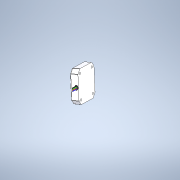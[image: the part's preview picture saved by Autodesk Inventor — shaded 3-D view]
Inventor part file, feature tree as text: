
AUTODESK INVENTOR PART (.ipt)
format: ipt  version: 2021 (Build 250183000, 183)  size: 951,296 bytes
history: native  units: mm
features: extrude x13, sketch x5, hole x4, fillet x4, plane x2, chamfer x2, pattern_linear x1, projected_geometry x1
ambient origin geometry x8: Origin, YZ Plane, XZ Plane, XY Plane, X Axis, Y Axis, Z Axis, Center Point
bodies: Solid1 (feature_tree)
feature tree (32):
  sketch  "Sketch1"  dims[d0=7.0mm d1=22.0mm]
  extrude  "Extrusion1"  Depth=22.0mm
  extrude  "Extrusion2"  Depth=31.0mm
  extrude  "Extrusion3"  Depth=3.0mm
  plane  "Work Plane2"
  extrude  "Extrusion7"  Depth=3.0mm
  extrude  "Extrusion8"  Depth=10.0mm
  chamfer  "Chamfer1"  Distance=42.0mm
  pattern_linear  "Rectangular Pattern2"  Spacing1=135.0deg  [1 undecoded]
  hole  "Hole1"  [1 undecoded]
  hole  "Hole2"  [1 undecoded]
  hole  "Hole3"  [1 undecoded]
  hole  "Hole4"  [1 undecoded]
  extrude  "Extrusion9"  Depth=10.0mm TaperAngle=0.0deg
  fillet  "Fillet1"  Radius=2.0mm
  fillet  "Fillet2"  Radius=48.0mm
  chamfer  "Chamfer2"  [1 undecoded]
  fillet  "Fillet3"  Radius=28.0mm
  sketch  "Sketch6"  dims[d10=3.0mm d11=3.0mm]
  extrude  "Extrusion10"  Depth=10.0mm
  fillet  "Fillet4"  Radius=1.0mm
  extrude  "Extrusion11"  Depth=10.0mm
  extrude  "Extrusion12"  Depth=10.0mm
  extrude  "Extrusion13"  Depth=10.0mm
  extrude  "Extrusion14"  Depth=10.0mm
  extrude  "Extrusion15"  Depth=10.0mm
  plane  "Work Plane3"
  extrude  "Extrusion16"  Depth=10.0mm
  sketch  "Sketch4"  dims[d4=5.0mm d5=31.0mm]
  projected_geometry  "Projected Loop2"
  sketch  "Sketch5"  dims[d6=31.0mm d9=3.0mm]
  sketch  "Sketch11"  dims[d12=3.0mm d39=42.0mm d40=42.0mm d41=135.0deg d42=51.618795mm d43=51.618795mm d44=25.809398mm d45=25.809398mm d46=24.0mm d47=0.0mm d48=2.0mm d49=0.0mm d50=48.0mm d51=0.0mm d60=-10.0mm d126=28.0mm d127=0.0mm d128=1.0mm d129=1.0mm d130=1.0mm d131=1.0mm d132=0.5mm d134=0.5mm d135=0.5mm d136=0.5mm d137=0.5mm d138=1.0mm d139=1.0mm d140=0.5mm d141=0.0mm d145=0.125mm d146=2.0mm d147=45.0deg d148=560.0mm d150=0.5mm d151=10.0mm d152=10.0mm d153=6.0mm d154=6.0mm d155=4.0mm d156=2.0mm d157=90.0deg d158=3.0mm d159=0.0mm d160=10.0mm d161=10.0mm d162=6.0mm d163=6.0mm d164=4.0mm d165=2.0mm d166=90.0deg d167=3.0mm d168=0.0mm d169=10.0mm d170=10.0mm d171=6.0mm d172=6.0mm d173=4.0mm d174=2.0mm d175=90.0deg d176=3.0mm d177=0.0mm d178=10.0mm d179=10.0mm d180=6.0mm d181=6.0mm d182=4.0mm d183=2.0mm d184=90.0deg d185=3.0mm d186=0.0mm d187=48.0mm d188=0.0mm d189=47.0mm d190=0.0mm d191=1.0mm d192=1.0mm d193=0.5mm d194=2.0mm d195=45.0deg d196=0.5mm d197=1.2mm d198=40.0mm d200=1.2mm d201=10.0mm d203=10.0mm d205=2.5mm d206=2.5mm d207=1.0mm d208=0.0mm d209=0.3mm d210=10.0mm d211=0.0mm d212=10.0mm d213=0.0mm d214=10.0mm d215=0.0mm d216=10.0mm d217=0.0mm d218=0.2mm d219=5.0mm d220=0.0mm d221=0.0mm d225=0.0mm d226=77.321962mm d227=95.435162mm d228=46.65084mm d229=46.129669mm d230=100.0mm d231=0.0mm]
note: 6 required parameter values undecoded (feature->parameter linkage not recoverable at this tier; creation-order binding heuristic only, values carry confidence <= 0.55)
